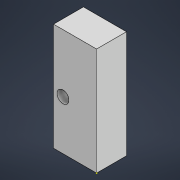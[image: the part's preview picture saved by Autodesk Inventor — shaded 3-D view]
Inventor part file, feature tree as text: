
AUTODESK INVENTOR PART (.ipt)
format: ipt  version: 2022.2 (Build 262287000, 287)  size: 90,112 bytes
history: native  units: in
note: dims shown in document units (in); Inventor stores cm internally (conversion verified against a paired STEP export)
features: sketch x3, extrude x2
ambient origin geometry x8: Origin, YZ Plane, XZ Plane, XY Plane, X Axis, Y Axis, Z Axis, Center Point
bodies: Solid1 (feature_tree)
feature tree (5):
  extrude  "Extrusion1"  Depth=1.0in TaperAngle=0.0deg
  sketch  "Sketch2"
  extrude  "Extrusion2"  [1 undecoded]
  sketch  "Sketch1"  dims[d0=1.0in d1=0.0in d2=1.0in d3=0.0in]
  sketch  "Sketch3"
note: 1 required parameter value undecoded (feature->parameter linkage not recoverable at this tier; creation-order binding heuristic only, values carry confidence <= 0.55)
